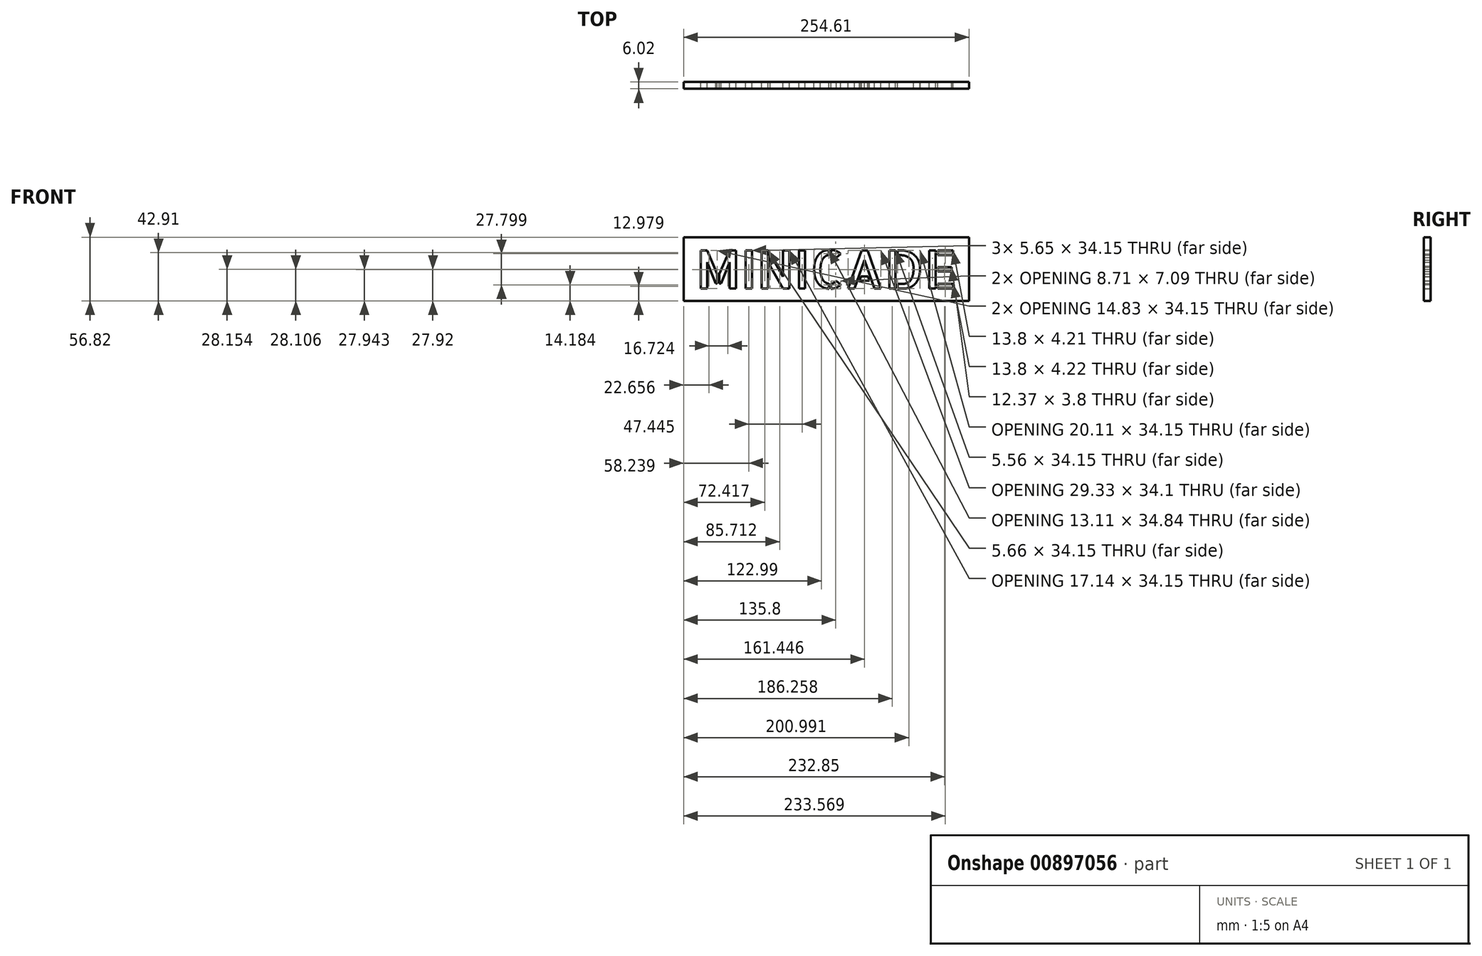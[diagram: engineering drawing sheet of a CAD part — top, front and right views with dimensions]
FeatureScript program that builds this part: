
annotation { "Feature Type Name" : "Feature", "Feature Type Description" : "" }
export const myFeature = defineFeature(function(context is Context, id is Id, definition is map)
    precondition{}
    {
        {
            var Q0;
            Q0=qCreatedBy(makeId("Front.planeOp"),FACE);
            var sketch = newSketch(context, id + "F0", { "sketchPlane" : qUnion([Q0])});
            skLineSegment(sketch, "E0.bottom", {"start": v(-3.74, 0) * mm, "end": v(250.87, 0) * mm});
            skLineSegment(sketch, "E0.top", {"start": v(-3.74, 56.82) * mm, "end": v(250.87, 56.82) * mm});
            skLineSegment(sketch, "E0.left", {"start": v(-3.74, 0) * mm, "end": v(-3.74, 56.82) * mm});
            skLineSegment(sketch, "E0.right", {"start": v(250.87, 0) * mm, "end": v(250.87, 56.82) * mm});
            skText(sketch, "E1", { "text": "MINICADE", "fontName": "AllertaStencil-Regular.ttf"});
            skPoint(sketch, "E2", {"position": v(123.57, 56.82) * mm});
            const initialGuessF0  = {"E1": [0.00724, 0.01087, 1, 0, 0.03416]};
            skSetInitialGuess(sketch, initialGuessF0);
            skSolve(sketch);
        }
        {
            var Q0;
            Q0=makeQuery(id+"F0.imprint","IMPRINT",FACE,{"disambiguationData":[TD([[makeQuery(id+"F0.imprint","IMPRINT",EDGE,{"derivedFrom":sQuery(id+"F0.wireOp",EDGE,"E0.bottom")}),1.0]])]});
            extrude(context, id + "F1", {"entities" : qUnion([Q0]), "depth" : 6.02 * mm, "offsetDistance" : 25.4 * mm});
        }
    });
